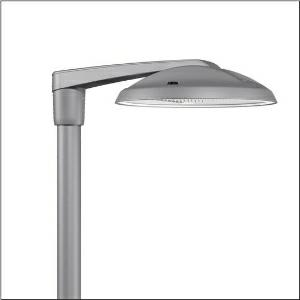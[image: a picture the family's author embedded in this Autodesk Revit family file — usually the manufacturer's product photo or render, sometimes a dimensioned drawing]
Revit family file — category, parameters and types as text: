
# Revit family: dl_r__50_iq_mini___st1_0a_5xa248d31v08me_e0eb
name_source: partatom
category: Lighting Fixtures
units: mm (PartAtom-declared; Revit-internal decimal feet)

## family parameters
Cut with Voids When Loaded = No
Host = Face
Light Source = No
Part Type = Normal
Room Calculation Point = No
Round Connector Dimension = Use Diameter
Shared = No

## types (1)
- --- (1 x LED, 15720 lm, 107 W, 3000K)
    Apparent Load = 107 VA
    CIE Flux Codes = 37 72 97 100 100
    Color Rendering = 70
    Color Temperature = 3000K
    Default Elevation = 1800 mm
    Description = DL® 50 iQ mini, mast luminaire, primary light control with lens, of PMMA, primary optical cover: cover, of toughened safety glass, transparent, light distribution: ST1.0a, light emission: direct distribution, primary light characteristic: asymmetric, installation type: post-top, side-entry, LED, High Power LED, rated luminous flux: 15.720lm, luminous efficacy: 147lm/W, light colour: 730, colour temperature: 3000K, control gear: iQ-Street Remote, D4i with power reduction, control: optimised constant luminous flux control (CLO 2.0), Desk-Remote (wireless, voltage-free reading and setting of iQ features in the workshop via application-optimized NFC function/RFID function), Light-Fading, Smart-Wire, Night-Set, Lumen-Switch, Temp-Guard, Auto-Match, Street-Remote, pre-setting: logarithmic dimming characteristic, mains connection: 230..240V, AC, 50/60Hz, connection cable pre-assembled, cable length: 10,5m, start of lifetime: 107W, end of service life: 113W, reduction: 47W, luminaire housing, of diecast aluminium, powder-coated, Siteco® metallic grey (DB 702S), inclination adjustable: 0°, 5°, 10° (post-top) | 0°, -5°, -10°, -15° (side-entry), please order mast post-top element or mast side-entry element separately, diameter: 500mm, height: 115mm, post-top: for spigot size d x l = 76 x 100mm; with reducer (optional accessory) 60 x 100mm | side-entry: for spigot size d x l = 60 x 100mm; with reducer (optional accessory) 42 x 100mm, mounting height: 4..6m, Smart Interface above, protection rating (complete): IP66, insulation class (complete): insulation class II (safety insulation), certification: CE, ENEC, ENEC+, VDE, impact resistance: IK08, permissible operating ambient temperature for outdoor applications: -25..+40°C, standard-compliant lighting for roads and squares, packaging unit: 1 piece

Light Distribution: ST1.0a
    Height = 115 mm
    Lamp = 1 x LED
    Lamp Light Flux = 15720 lm
    Lamp Power = 107 W
    Lamp count = 1
    Length = 500 mm
    Luminous efficacy = 147 lm/W
    Manufacturer = Siteco
    ModVariant = No
    Model = 5XA248D31V08ME
    Number of Poles = 1
    OnlyDefault = Yes
    Power Factor = 1
    Product Name = DL® 50 iQ mini | ST1.0a
    Product group = mast luminaire | pylon top
    ProductGroupID = 6100
    Protection Class = Protection class II
    Protection Degree = IP 66
    RLX_Detail_Level = 1
    RLX_Emergency_Light_Flux = 0 lm
    RLX_Emergency_Type = 0
    RLX_Emergency_Type_DB = No
    RlxData = <blob elided: 106709 chars, md5=39a8e505>
    Socket = socket
    Standby Power = 0 W
    System Light Flux = 15720 lm
    System Power = 107 W
    Type Comments = factory setting: luminous flux: 100 % | dim-lin: 254 | 565 mA
    Type Image = l_1251788.jpg
    URL = http://relux.com
    VarID = @adj_067652
    Voltage = 0 V
    Weight = 0.00 kg
    Width = 0 mm  [stored 0 ft]

note: [stored X ft] marks values corroborated as IEEE doubles in the binary element streams (Revit-internal decimal feet)

## geometry (parser evidence)
native form markers: Blend x4, Sweep x8
no freeform markers — native parametric forms only
